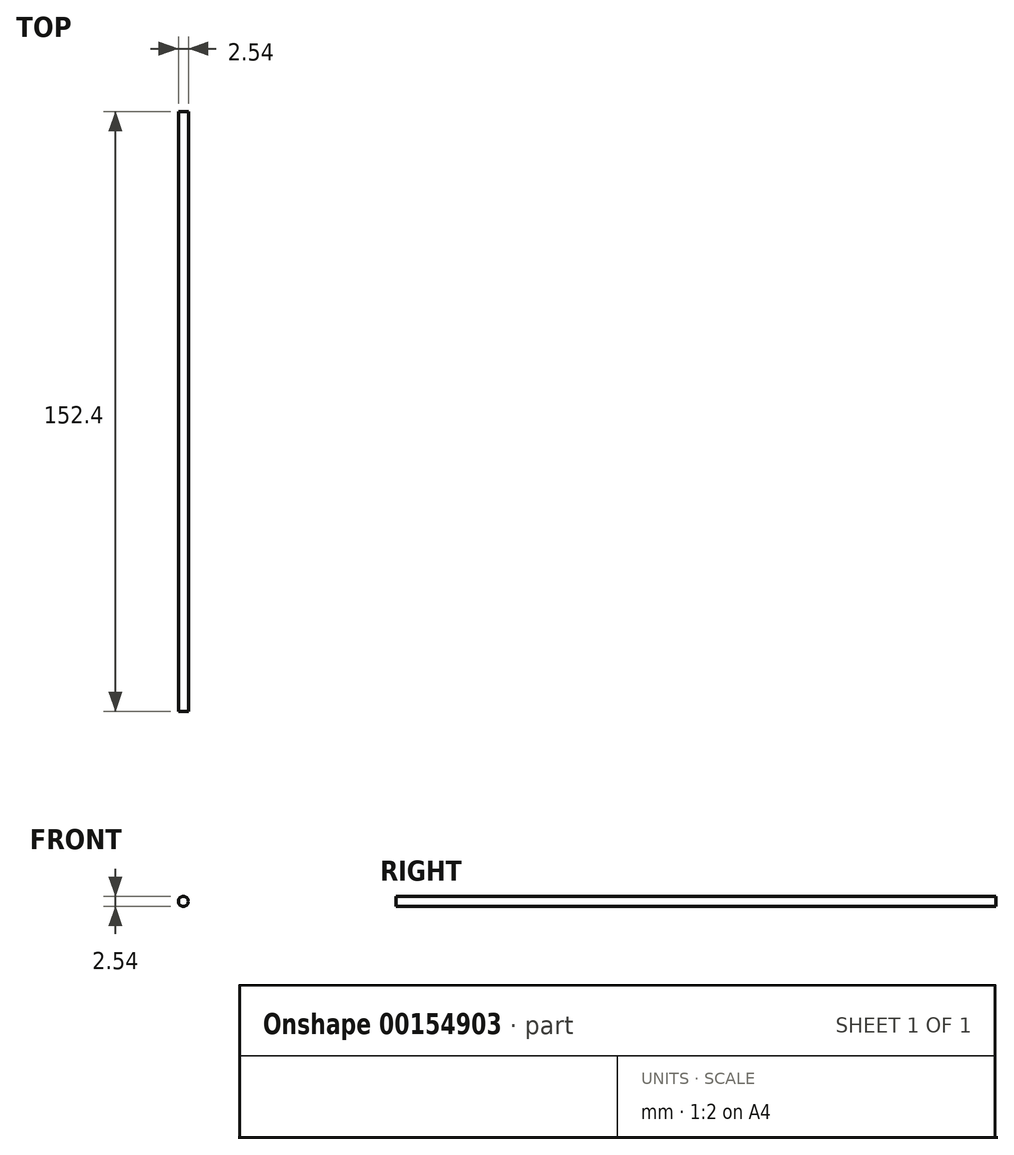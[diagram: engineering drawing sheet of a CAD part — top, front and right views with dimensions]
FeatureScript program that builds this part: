
annotation { "Feature Type Name" : "Feature", "Feature Type Description" : "" }
export const myFeature = defineFeature(function(context is Context, id is Id, definition is map)
    precondition{}
    {
        {
            var Q0;
            Q0=qCreatedBy(makeId("Front.planeOp"),FACE);
            var sketch = newSketch(context, id + "F0", { "sketchPlane" : qUnion([Q0])});
            skCircle(sketch, "E0", {"center": v(0, 0) * mm, "radius": 1.27 * mm});
            skSolve(sketch);
        }
        {
            var Q0;
            Q0=makeQuery(id+"F0.imprint","IMPRINT",FACE,{"disambiguationData":[TD([[makeQuery(id+"F0.imprint","IMPRINT",EDGE,{"derivedFrom":sQuery(id+"F0.wireOp",EDGE,"E0")}),1.0]])]});
            extrude(context, id + "F1", {"entities" : qUnion([Q0]), "depth" : 152.4 * mm});
        }
    });
